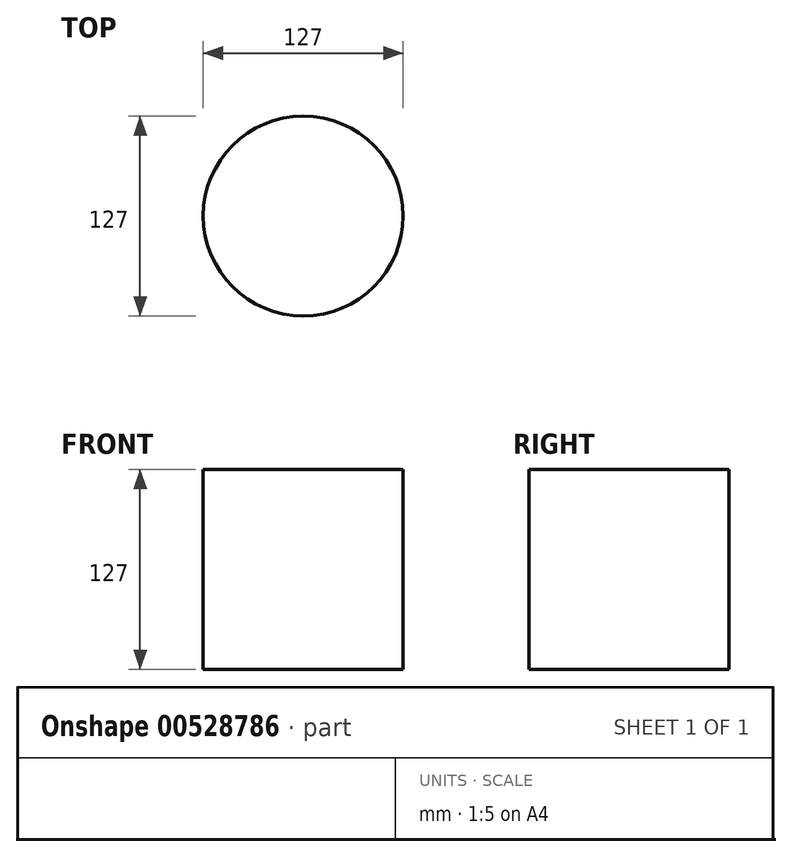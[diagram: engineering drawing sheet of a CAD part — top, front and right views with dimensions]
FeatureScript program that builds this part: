
annotation { "Feature Type Name" : "Feature", "Feature Type Description" : "" }
export const myFeature = defineFeature(function(context is Context, id is Id, definition is map)
    precondition{}
    {
        {
            var Q0;
            Q0=qCreatedBy(makeId("Top.planeOp"),FACE);
            var sketch = newSketch(context, id + "F0", { "sketchPlane" : qUnion([Q0])});
            skCircle(sketch, "E0", {"center": v(0, 0) * mm, "radius": 63.5 * mm});
            skSolve(sketch);
        }
        {
            var Q0;
            Q0 = qSketchRegion(id + "F0", true);
            extrude(context, id + "F1", {"entities" : qUnion([Q0]), "depth" : 127 * mm, "offsetDistance" : 25.4 * mm});
        }
        {
            var Q0;
            Q0=qCreatedBy(makeId("Front.planeOp"),FACE);
            var sketch = newSketch(context, id + "F2", { "sketchPlane" : qUnion([Q0])});
            skLineSegment(sketch, "E1", {"start": v(63.5, 127) * mm, "end": v(63.48, 127) * mm});
            skLineSegment(sketch, "E2", {"start": v(63.48, 127) * mm, "end": v(36.99, 148.72) * mm});
            skLineSegment(sketch, "E3", {"start": v(36.99, 148.72) * mm, "end": v(0, 148.72) * mm});
            skLineSegment(sketch, "E4", {"start": v(0, 148.72) * mm, "end": v(0, 127) * mm});
            skLineSegment(sketch, "E5", {"start": v(0, 127) * mm, "end": v(63.5, 127) * mm});
            skSolve(sketch);
        }
        {
            var Q0;
            Q0=sQuery(id+"F2.wireOp",EDGE,"E3");
            var Q1;
            Q1=sQuery(id+"F2.wireOp",EDGE,"E2");
            var Q2;
            Q2=sQuery(id+"F2.wireOp",EDGE,"E5");
            var Q3;
            Q3=sQuery(id+"F2.wireOp",EDGE,"E4");
            revolve(context, id + "F3", {"bodyType" : ToolBodyType.SURFACE, "surfaceEntities" : qUnion([Q0, Q1, Q2]), "axis" : qUnion([Q3]), "revolveType" : RevolveType.FULL});
        }
    });
